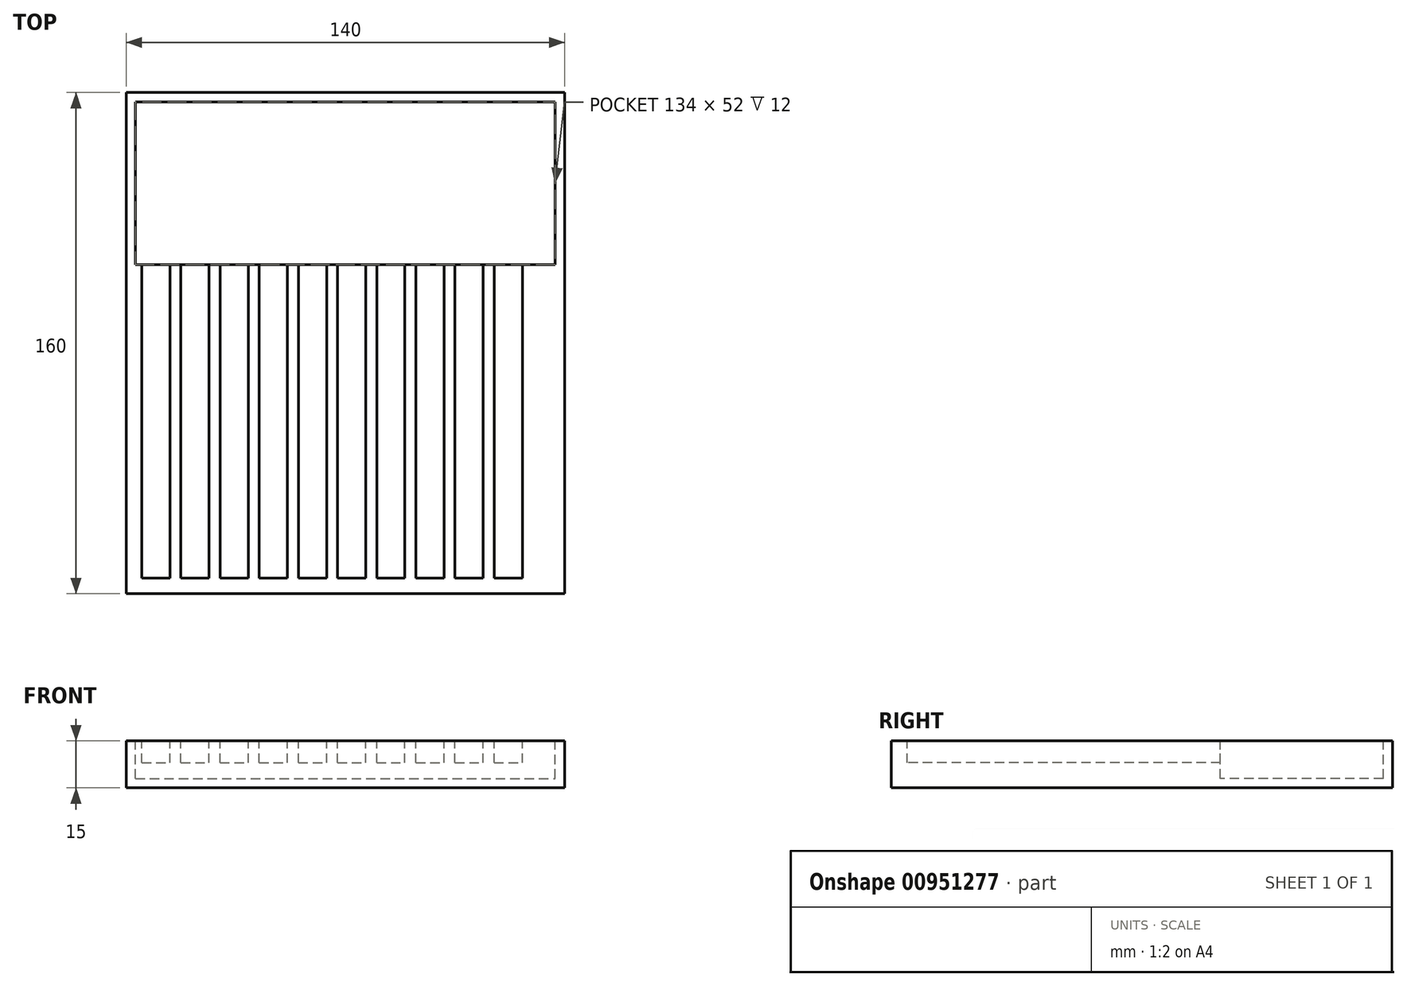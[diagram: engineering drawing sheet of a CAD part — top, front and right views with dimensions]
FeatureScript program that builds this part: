
annotation { "Feature Type Name" : "Feature", "Feature Type Description" : "" }
export const myFeature = defineFeature(function(context is Context, id is Id, definition is map)
    precondition{}
    {
        {
            var Q0;
            Q0=qCreatedBy(makeId("Top.planeOp"),FACE);
            var sketch = newSketch(context, id + "F0", { "sketchPlane" : qUnion([Q0])});
            skLineSegment(sketch, "E0", {"start": v(-55.66, 54.52) * mm, "end": v(84.34, 54.52) * mm});
            skLineSegment(sketch, "E1", {"start": v(84.34, 54.52) * mm, "end": v(84.34, -105.48) * mm});
            skLineSegment(sketch, "E2", {"start": v(-55.66, 54.52) * mm, "end": v(-55.66, -105.48) * mm});
            skLineSegment(sketch, "E3", {"start": v(-55.66, -105.48) * mm, "end": v(84.34, -105.48) * mm});
            skSolve(sketch);
        }
        {
            var Q0;
            Q0 = qSketchRegion(id + "F0", true);
            var Q1;
            Q1=makeQuery(id+"F0.imprint","IMPRINT",FACE,{"disambiguationData":[TD([[makeQuery(id+"F0.imprint","IMPRINT",EDGE,{"derivedFrom":sQuery(id+"F0.wireOp",EDGE,"E0")}),-1.0]])]});
            extrude(context, id + "F1", {"entities" : qUnion([Q0, Q1]), "depth" : 15 * mm, "offsetDistance" : 25 * mm});
        }
        {
            var Q0;
            Q0=makeQuery(id+"F1.opExtrude","CAP_FACE",FACE,{"disambiguationData":[OSD([sQuery(id+"F0.wireOp",EDGE,"E0"),sQuery(id+"F0.wireOp",EDGE,"E1"),sQuery(id+"F0.wireOp",EDGE,"E2"),sQuery(id+"F0.wireOp",EDGE,"E3")])],"isStart":false});
            var sketch = newSketch(context, id + "F2", { "sketchPlane" : qUnion([Q0])});
            skLineSegment(sketch, "E4", {"start": v(-55.66, 54.52) * mm, "end": v(-55.66, 51.52) * mm});
            skLineSegment(sketch, "E5", {"start": v(-55.66, 51.52) * mm, "end": v(84.34, 51.52) * mm});
            skLineSegment(sketch, "E6", {"start": v(-55.66, 54.52) * mm, "end": v(-52.66, 54.52) * mm});
            skLineSegment(sketch, "E7", {"start": v(84.34, 54.52) * mm, "end": v(81.34, 54.52) * mm});
            skLineSegment(sketch, "E8", {"start": v(81.34, 54.52) * mm, "end": v(81.34, -105.48) * mm});
            skPoint(sketch, "E8.endSnap0", {"position": v(14.34, -105.48) * mm});
            skLineSegment(sketch, "E9", {"start": v(-52.66, 54.52) * mm, "end": v(-52.66, -105.48) * mm});
            skLineSegment(sketch, "E10", {"start": v(-55.66, -105.48) * mm, "end": v(-55.66, -102.48) * mm});
            skLineSegment(sketch, "E11", {"start": v(-55.66, -102.48) * mm, "end": v(84.34, -102.48) * mm});
            skLineSegment(sketch, "E12", {"start": v(-52.66, 51.52) * mm, "end": v(-52.66, -0.48) * mm});
            skLineSegment(sketch, "E13", {"start": v(-52.66, -0.48) * mm, "end": v(81.34, -0.48) * mm});
            skSolve(sketch);
        }
        {
            var Q0;
            {var subQ5=sQuery(id+"F2.wireOp",EDGE,"E13");Q0=makeQuery(id+"F2.imprint","IMPRINT",FACE,{"disambiguationData":[TD([[makeQuery(id+"F2.imprint","IMPRINT",EDGE,{"derivedFrom":subQ5}),1.0]])]});}
            extrude(context, id + "F3", {"entities" : qUnion([Q0]), "operationType" : NewBodyOperationType.REMOVE, "oppositeDirection" : true, "depth" : 12 * mm, "offsetDistance" : 25 * mm});
        }
        {
            var Q0;
            Q0=makeQuery(id+"F1.opExtrude","CAP_FACE",FACE,{"disambiguationData":[OSD([sQuery(id+"F0.wireOp",EDGE,"E0"),sQuery(id+"F0.wireOp",EDGE,"E1"),sQuery(id+"F0.wireOp",EDGE,"E2"),sQuery(id+"F0.wireOp",EDGE,"E3")])],"isStart":false});
            var sketch = newSketch(context, id + "F4", { "sketchPlane" : qUnion([Q0])});
            skLineSegment(sketch, "E14", {"start": v(-52.66, -0.48) * mm, "end": v(-50.66, -0.48) * mm});
            skLineSegment(sketch, "E15", {"start": v(-50.66, -0.48) * mm, "end": v(-50.66, -100.48) * mm});
            skLineSegment(sketch, "E16", {"start": v(-50.66, -100.48) * mm, "end": v(-41.66, -100.48) * mm});
            skLineSegment(sketch, "E17", {"start": v(-41.66, -100.48) * mm, "end": v(-41.66, -0.48) * mm});
            skLineSegment(sketch, "E18", {"start": v(-41.66, -0.48) * mm, "end": v(-50.66, -0.48) * mm});
            skLineSegment(sketch, "E19", {"start": v(-41.66, -0.48) * mm, "end": v(-38.16, -0.48) * mm});
            skLineSegment(sketch, "E20", {"start": v(-38.16, -0.48) * mm, "end": v(-38.16, -100.48) * mm});
            skLineSegment(sketch, "E21", {"start": v(-38.16, -100.48) * mm, "end": v(-29.16, -100.48) * mm});
            skLineSegment(sketch, "E22", {"start": v(-29.16, -100.48) * mm, "end": v(-29.16, -0.48) * mm});
            skLineSegment(sketch, "E23", {"start": v(-29.16, -0.48) * mm, "end": v(-25.66, -0.48) * mm});
            skLineSegment(sketch, "E24", {"start": v(-25.66, -0.48) * mm, "end": v(-25.66, -100.48) * mm});
            skLineSegment(sketch, "E25", {"start": v(-25.66, -100.48) * mm, "end": v(-16.66, -100.48) * mm});
            skLineSegment(sketch, "E26", {"start": v(-16.66, -100.48) * mm, "end": v(-16.66, -0.48) * mm});
            skLineSegment(sketch, "E27", {"start": v(-16.66, -0.48) * mm, "end": v(-13.16, -0.48) * mm});
            skLineSegment(sketch, "E28", {"start": v(-13.16, -0.48) * mm, "end": v(-13.16, -100.48) * mm});
            skLineSegment(sketch, "E29", {"start": v(-13.16, -100.48) * mm, "end": v(-4.16, -100.48) * mm});
            skLineSegment(sketch, "E30", {"start": v(-4.16, -100.48) * mm, "end": v(-4.16, -0.48) * mm});
            skLineSegment(sketch, "E31", {"start": v(-4.16, -0.48) * mm, "end": v(-0.66, -0.48) * mm});
            skLineSegment(sketch, "E32", {"start": v(-0.66, -0.48) * mm, "end": v(-0.66, -100.48) * mm});
            skLineSegment(sketch, "E33", {"start": v(-0.66, -100.48) * mm, "end": v(8.34, -100.48) * mm});
            skLineSegment(sketch, "E34", {"start": v(8.34, -100.48) * mm, "end": v(8.34, -0.48) * mm});
            skLineSegment(sketch, "E35", {"start": v(8.34, -0.48) * mm, "end": v(11.84, -0.48) * mm});
            skLineSegment(sketch, "E36", {"start": v(11.84, -0.48) * mm, "end": v(11.84, -100.48) * mm});
            skLineSegment(sketch, "E37", {"start": v(11.84, -100.48) * mm, "end": v(20.84, -100.48) * mm});
            skLineSegment(sketch, "E38", {"start": v(20.84, -100.48) * mm, "end": v(20.84, -0.48) * mm});
            skLineSegment(sketch, "E39", {"start": v(20.84, -0.48) * mm, "end": v(24.34, -0.48) * mm});
            skLineSegment(sketch, "E40", {"start": v(24.34, -0.48) * mm, "end": v(24.34, -100.48) * mm});
            skLineSegment(sketch, "E41", {"start": v(24.34, -100.48) * mm, "end": v(33.34, -100.48) * mm});
            skLineSegment(sketch, "E42", {"start": v(33.34, -100.48) * mm, "end": v(33.34, -0.48) * mm});
            skLineSegment(sketch, "E43", {"start": v(33.34, -0.48) * mm, "end": v(36.84, -0.48) * mm});
            skLineSegment(sketch, "E44", {"start": v(36.84, -0.48) * mm, "end": v(36.84, -100.48) * mm});
            skLineSegment(sketch, "E45", {"start": v(36.84, -100.48) * mm, "end": v(45.84, -100.48) * mm});
            skLineSegment(sketch, "E46", {"start": v(45.84, -100.48) * mm, "end": v(45.84, -0.48) * mm});
            skLineSegment(sketch, "E47", {"start": v(45.84, -0.48) * mm, "end": v(49.34, -0.48) * mm});
            skLineSegment(sketch, "E48", {"start": v(49.34, -0.48) * mm, "end": v(49.34, -100.48) * mm});
            skLineSegment(sketch, "E49", {"start": v(49.34, -100.48) * mm, "end": v(58.34, -100.48) * mm});
            skLineSegment(sketch, "E50", {"start": v(58.34, -100.48) * mm, "end": v(58.34, -0.48) * mm});
            skLineSegment(sketch, "E51", {"start": v(58.34, -0.48) * mm, "end": v(61.84, -0.48) * mm});
            skLineSegment(sketch, "E52", {"start": v(61.84, -0.48) * mm, "end": v(61.84, -100.48) * mm});
            skLineSegment(sketch, "E53", {"start": v(61.84, -100.48) * mm, "end": v(70.84, -100.48) * mm});
            skLineSegment(sketch, "E54", {"start": v(70.84, -100.48) * mm, "end": v(70.84, -0.48) * mm});
            skSolve(sketch);
        }
        {
            var Q0;
            Q0 = qSketchRegion(id + "F4", true);
            var Q1;
            {var subQ0=sQuery(id+"F4.wireOp",EDGE,"E20");Q1=makeQuery(id+"F4.imprint","IMPRINT",FACE,{"disambiguationData":[TD([[makeQuery(id+"F4.imprint","IMPRINT",EDGE,{"derivedFrom":subQ0}),1.0]])]});}
            var Q2;
            {var subQ0=sQuery(id+"F4.wireOp",EDGE,"E28");Q2=makeQuery(id+"F4.imprint","IMPRINT",FACE,{"disambiguationData":[TD([[makeQuery(id+"F4.imprint","IMPRINT",EDGE,{"derivedFrom":subQ0}),1.0]])]});}
            var Q3;
            {var subQ0=sQuery(id+"F4.wireOp",EDGE,"E32");Q3=makeQuery(id+"F4.imprint","IMPRINT",FACE,{"disambiguationData":[TD([[makeQuery(id+"F4.imprint","IMPRINT",EDGE,{"derivedFrom":subQ0}),1.0]])]});}
            var Q4;
            {var subQ0=sQuery(id+"F4.wireOp",EDGE,"E40");Q4=makeQuery(id+"F4.imprint","IMPRINT",FACE,{"disambiguationData":[TD([[makeQuery(id+"F4.imprint","IMPRINT",EDGE,{"derivedFrom":subQ0}),1.0]])]});}
            var Q5;
            {var subQ0=sQuery(id+"F4.wireOp",EDGE,"E44");Q5=makeQuery(id+"F4.imprint","IMPRINT",FACE,{"disambiguationData":[TD([[makeQuery(id+"F4.imprint","IMPRINT",EDGE,{"derivedFrom":subQ0}),1.0]])]});}
            var Q6;
            {var subQ0=sQuery(id+"F4.wireOp",EDGE,"E48");Q6=makeQuery(id+"F4.imprint","IMPRINT",FACE,{"disambiguationData":[TD([[makeQuery(id+"F4.imprint","IMPRINT",EDGE,{"derivedFrom":subQ0}),1.0]])]});}
            var Q7;
            {var subQ0=sQuery(id+"F4.wireOp",EDGE,"E52");Q7=makeQuery(id+"F4.imprint","IMPRINT",FACE,{"disambiguationData":[TD([[makeQuery(id+"F4.imprint","IMPRINT",EDGE,{"derivedFrom":subQ0}),1.0]])]});}
            var Q8;
            {var subQ0=sQuery(id+"F4.wireOp",EDGE,"E36");Q8=makeQuery(id+"F4.imprint","IMPRINT",FACE,{"disambiguationData":[TD([[makeQuery(id+"F4.imprint","IMPRINT",EDGE,{"derivedFrom":subQ0}),1.0]])]});}
            var Q9;
            {var subQ0=sQuery(id+"F4.wireOp",EDGE,"E24");Q9=makeQuery(id+"F4.imprint","IMPRINT",FACE,{"disambiguationData":[TD([[makeQuery(id+"F4.imprint","IMPRINT",EDGE,{"derivedFrom":subQ0}),1.0]])]});}
            extrude(context, id + "F5", {"entities" : qUnion([Q0, Q1, Q2, Q3, Q4, Q5, Q6, Q7, Q8, Q9]), "operationType" : NewBodyOperationType.REMOVE, "oppositeDirection" : true, "depth" : 7 * mm, "offsetDistance" : 25 * mm});
        }
    });
